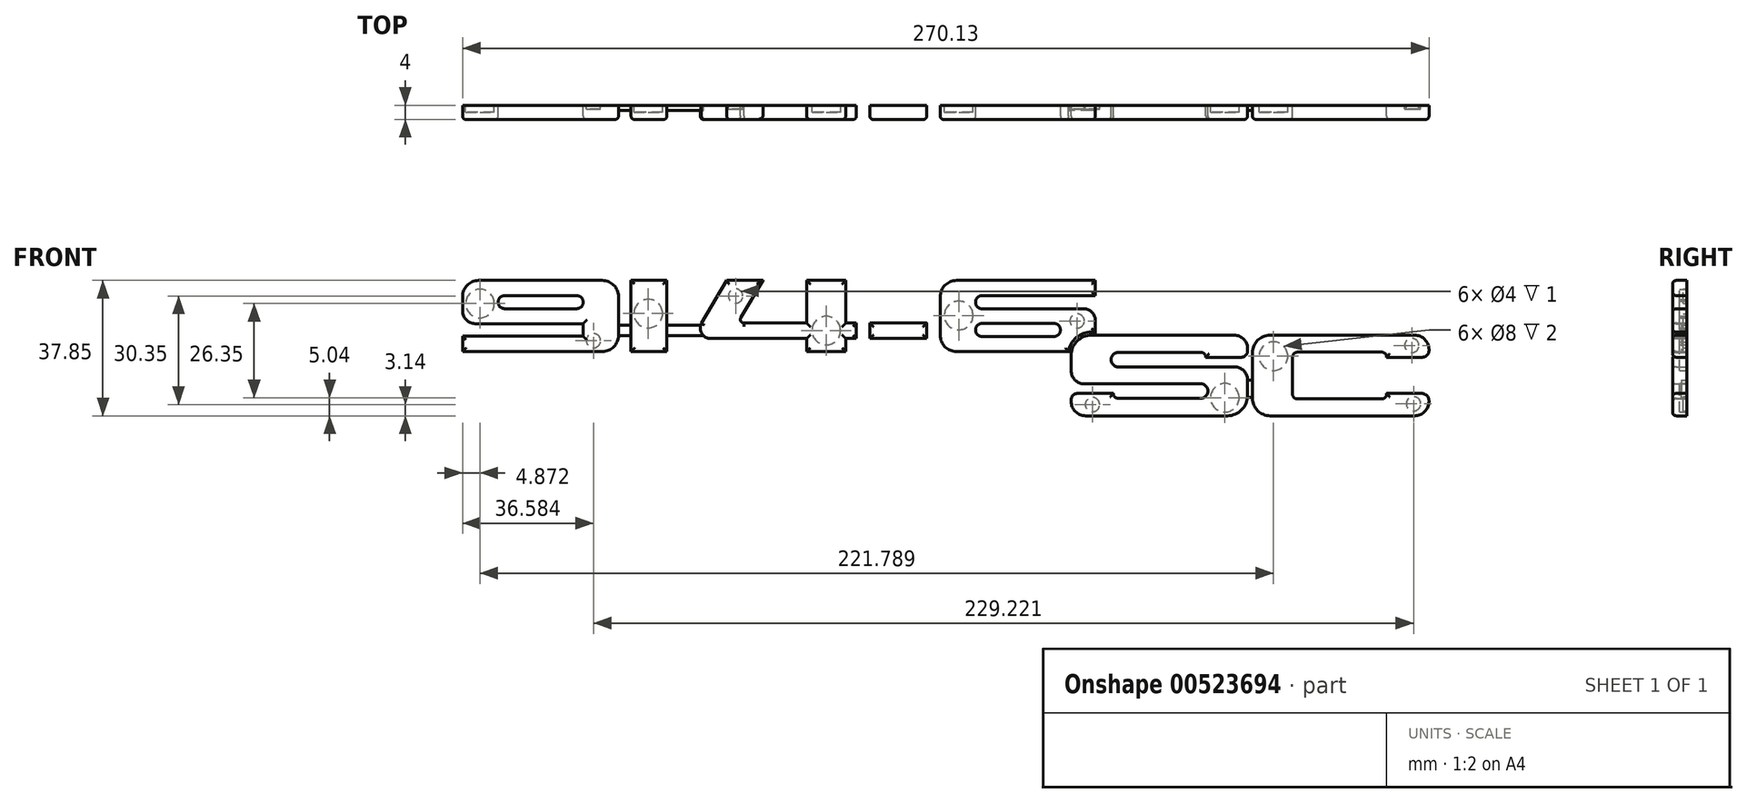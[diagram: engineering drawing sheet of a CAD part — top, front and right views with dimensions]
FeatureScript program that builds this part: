
annotation { "Feature Type Name" : "Feature", "Feature Type Description" : "" }
export const myFeature = defineFeature(function(context is Context, id is Id, definition is map)
    precondition{}
    {
        {
            var Q0;
            Q0=qCreatedBy(makeId("Front.planeOp"),FACE);
            var sketch = newSketch(context, id + "F0", { "sketchPlane" : qUnion([Q0])});
            skPoint(sketch, "E0", {"position": v(-109.13, 31.6) * mm});
            skPoint(sketch, "E1", {"position": v(-109.13, 11.72) * mm});
            skPoint(sketch, "E2", {"position": v(-65.54, 11.72) * mm});
            skPoint(sketch, "E3", {"position": v(-65.54, 31.6) * mm});
            skLineSegment(sketch, "E4.bottom", {"start": v(-104.63, 31.6) * mm, "end": v(-70.04, 31.6) * mm});
            skLineSegment(sketch, "E4.top", {"start": v(-109.13, 11.72) * mm, "end": v(-70.04, 11.72) * mm});
            skLineSegment(sketch, "E4.left", {"start": v(-109.13, 27.1) * mm, "end": v(-109.13, 23.04) * mm});
            skLineSegment(sketch, "E4.right", {"start": v(-65.54, 27.1) * mm, "end": v(-65.54, 16.22) * mm});
            skLineSegment(sketch, "E5.bottom", {"start": v(-109.13, 15.99) * mm, "end": v(-75.41, 15.99) * mm});
            skLineSegment(sketch, "E5.top", {"start": v(-105.62, 19.53) * mm, "end": v(-75.41, 19.53) * mm});
            skLineSegment(sketch, "E5.right", {"start": v(-75.41, 15.99) * mm, "end": v(-75.41, 19.53) * mm});
            skLineSegment(sketch, "E6.bottom", {"start": v(-77.15, 23.72) * mm, "end": v(-97.43, 23.72) * mm});
            skLineSegment(sketch, "E6.top", {"start": v(-77.15, 27.36) * mm, "end": v(-97.43, 27.36) * mm});
            skLineSegment(sketch, "E6.left", {"start": v(-75.41, 25.46) * mm, "end": v(-75.41, 25.62) * mm});
            skLineSegment(sketch, "E6.right", {"start": v(-99.16, 25.46) * mm, "end": v(-99.16, 25.62) * mm});
            skArc(sketch, "E7.filletArc", {"start": v(-104.63, 31.6) * mm, "mid": v(-107.81, 30.29) * mm, "end": v(-109.13, 27.1) * mm});
            skArc(sketch, "E8.filletArc", {"start": v(-65.54, 27.1) * mm, "mid": v(-66.86, 30.29) * mm, "end": v(-70.04, 31.6) * mm});
            skArc(sketch, "E9.filletArc", {"start": v(-70.04, 11.72) * mm, "mid": v(-66.86, 13.04) * mm, "end": v(-65.54, 16.22) * mm});
            skPoint(sketch, "E10.visualSharp", {"position": v(-99.16, 27.36) * mm});
            skArc(sketch, "E10.filletArc", {"start": v(-97.43, 27.36) * mm, "mid": v(-98.65, 26.85) * mm, "end": v(-99.16, 25.62) * mm});
            skPoint(sketch, "E11.visualSharp", {"position": v(-99.16, 23.72) * mm});
            skArc(sketch, "E11.filletArc", {"start": v(-99.16, 25.46) * mm, "mid": v(-98.65, 24.23) * mm, "end": v(-97.43, 23.72) * mm});
            skPoint(sketch, "E12.visualSharp", {"position": v(-75.41, 27.36) * mm});
            skArc(sketch, "E12.filletArc", {"start": v(-75.41, 25.62) * mm, "mid": v(-75.92, 26.85) * mm, "end": v(-77.15, 27.36) * mm});
            skPoint(sketch, "E13.visualSharp", {"position": v(-75.41, 23.72) * mm});
            skArc(sketch, "E13.filletArc", {"start": v(-77.15, 23.72) * mm, "mid": v(-75.92, 24.23) * mm, "end": v(-75.41, 25.46) * mm});
            skLineSegment(sketch, "E14.trimOffspring", {"start": v(-109.13, 15.99) * mm, "end": v(-109.13, 11.72) * mm});
            skPoint(sketch, "E15.visualSharp", {"position": v(-109.13, 19.53) * mm});
            skArc(sketch, "E15.filletArc", {"start": v(-109.13, 23.04) * mm, "mid": v(-108.1, 20.56) * mm, "end": v(-105.62, 19.53) * mm});
            skLineSegment(sketch, "E16", {"start": v(-62.04, 31.6) * mm, "end": v(-52.01, 31.6) * mm});
            skLineSegment(sketch, "E17", {"start": v(-62.04, 11.72) * mm, "end": v(-52.01, 11.72) * mm});
            skLineSegment(sketch, "E18.left", {"start": v(-62.04, 31.6) * mm, "end": v(-62.04, 11.72) * mm});
            skLineSegment(sketch, "E18.right", {"start": v(-52.01, 31.6) * mm, "end": v(-52.01, 11.72) * mm});
            skLineSegment(sketch, "E19", {"start": v(-31.25, 31.6) * mm, "end": v(-25.18, 31.6) * mm});
            skLineSegment(sketch, "E20.bottom", {"start": v(-12.94, 31.6) * mm, "end": v(-2.03, 31.6) * mm});
            skLineSegment(sketch, "E20.top", {"start": v(-12.94, 11.72) * mm, "end": v(-2.03, 11.72) * mm});
            skLineSegment(sketch, "E20.left", {"start": v(-12.94, 31.6) * mm, "end": v(-12.94, 19.68) * mm});
            skLineSegment(sketch, "E20.right", {"start": v(-2.03, 31.6) * mm, "end": v(-2.03, 19.68) * mm});
            skLineSegment(sketch, "E21.bottom", {"start": v(0.96, 19.68) * mm, "end": v(-2.03, 19.68) * mm});
            skLineSegment(sketch, "E21.top", {"start": v(0.96, 15.35) * mm, "end": v(-2.03, 15.35) * mm});
            skLineSegment(sketch, "E21.left", {"start": v(0.96, 19.68) * mm, "end": v(0.96, 15.35) * mm});
            skLineSegment(sketch, "E22", {"start": v(-35.26, 31.6) * mm, "end": v(-42.35, 19.59) * mm});
            skLineSegment(sketch, "E23", {"start": v(-25.18, 31.6) * mm, "end": v(-31.35, 21.25) * mm});
            skPoint(sketch, "E24", {"position": v(-30.43, 19.68) * mm});
            skLineSegment(sketch, "E25.trimOffspring", {"start": v(-12.94, 15.35) * mm, "end": v(-12.94, 11.72) * mm});
            skLineSegment(sketch, "E26.trimOffspring", {"start": v(-12.94, 15.35) * mm, "end": v(-39.77, 15.35) * mm});
            skLineSegment(sketch, "E27.trimOffspring", {"start": v(-2.03, 15.35) * mm, "end": v(-2.03, 11.72) * mm});
            skLineSegment(sketch, "E28.trimOffspring", {"start": v(-12.94, 19.68) * mm, "end": v(-30.43, 19.68) * mm});
            skLineSegment(sketch, "E29.trimOffspring", {"start": v(-35.26, 31.6) * mm, "end": v(-31.25, 31.6) * mm});
            skArc(sketch, "E30", {"start": v(-42.35, 19.59) * mm, "mid": v(-42.25, 16.75) * mm, "end": v(-39.77, 15.35) * mm});
            skArc(sketch, "E31", {"start": v(-31.35, 21.25) * mm, "mid": v(-31.35, 20.2) * mm, "end": v(-30.43, 19.68) * mm});
            skLineSegment(sketch, "E32", {"start": v(28.93, 31.6) * mm, "end": v(67.75, 31.6) * mm});
            skLineSegment(sketch, "E33", {"start": v(28.93, 11.72) * mm, "end": v(60.09, 11.72) * mm});
            skLineSegment(sketch, "E34.bottom", {"start": v(4.7, 19.69) * mm, "end": v(20.61, 19.69) * mm});
            skLineSegment(sketch, "E34.top", {"start": v(4.7, 15.35) * mm, "end": v(20.61, 15.35) * mm});
            skLineSegment(sketch, "E34.left", {"start": v(4.7, 19.69) * mm, "end": v(4.7, 15.35) * mm});
            skLineSegment(sketch, "E34.right", {"start": v(20.61, 19.69) * mm, "end": v(20.61, 15.35) * mm});
            skLineSegment(sketch, "E35", {"start": v(24.38, 26.4) * mm, "end": v(24.38, 16.28) * mm});
            skLineSegment(sketch, "E36", {"start": v(24.38, 26.4) * mm, "end": v(24.38, 27.06) * mm});
            skLineSegment(sketch, "E37", {"start": v(67.75, 31.6) * mm, "end": v(67.75, 27.39) * mm});
            skLineSegment(sketch, "E38.bottom", {"start": v(67.75, 27.39) * mm, "end": v(36.1, 27.39) * mm});
            skLineSegment(sketch, "E38.top", {"start": v(64.5, 23.67) * mm, "end": v(36.1, 23.67) * mm});
            skLineSegment(sketch, "E38.right", {"start": v(34.28, 25.56) * mm, "end": v(34.28, 25.5) * mm});
            skLineSegment(sketch, "E39.bottom", {"start": v(36.1, 19.61) * mm, "end": v(56.17, 19.61) * mm});
            skLineSegment(sketch, "E39.top", {"start": v(36.1, 15.93) * mm, "end": v(56.17, 15.93) * mm});
            skLineSegment(sketch, "E39.left", {"start": v(34.28, 17.78) * mm, "end": v(34.28, 17.76) * mm});
            skLineSegment(sketch, "E39.right", {"start": v(58, 17.78) * mm, "end": v(58, 17.76) * mm});
            skLineSegment(sketch, "E40.trimOffspring", {"start": v(67.75, 20.42) * mm, "end": v(67.75, 17.15) * mm});
            skPoint(sketch, "E41.visualSharp", {"position": v(24.38, 31.6) * mm});
            skArc(sketch, "E41.filletArc", {"start": v(28.93, 31.6) * mm, "mid": v(25.71, 30.27) * mm, "end": v(24.38, 27.06) * mm});
            skPoint(sketch, "E42.visualSharp", {"position": v(24.38, 11.72) * mm});
            skArc(sketch, "E42.filletArc", {"start": v(24.38, 16.28) * mm, "mid": v(25.71, 13.06) * mm, "end": v(28.93, 11.72) * mm});
            skPoint(sketch, "E43.visualSharp", {"position": v(67.75, 23.67) * mm});
            skArc(sketch, "E43.filletArc", {"start": v(67.75, 20.42) * mm, "mid": v(66.8, 22.72) * mm, "end": v(64.5, 23.67) * mm});
            skPoint(sketch, "E44.visualSharp", {"position": v(34.28, 27.39) * mm});
            skArc(sketch, "E44.filletArc", {"start": v(36.1, 27.39) * mm, "mid": v(34.81, 26.85) * mm, "end": v(34.28, 25.56) * mm});
            skPoint(sketch, "E45.visualSharp", {"position": v(34.28, 23.67) * mm});
            skArc(sketch, "E45.filletArc", {"start": v(34.28, 25.5) * mm, "mid": v(34.81, 24.21) * mm, "end": v(36.1, 23.67) * mm});
            skPoint(sketch, "E46.visualSharp", {"position": v(34.28, 19.61) * mm});
            skArc(sketch, "E46.filletArc", {"start": v(36.1, 19.61) * mm, "mid": v(34.81, 19.08) * mm, "end": v(34.28, 17.78) * mm});
            skPoint(sketch, "E47.visualSharp", {"position": v(34.28, 15.93) * mm});
            skArc(sketch, "E47.filletArc", {"start": v(34.28, 17.76) * mm, "mid": v(34.81, 16.47) * mm, "end": v(36.1, 15.93) * mm});
            skPoint(sketch, "E48.visualSharp", {"position": v(58, 19.61) * mm});
            skArc(sketch, "E48.filletArc", {"start": v(58, 17.78) * mm, "mid": v(57.46, 19.08) * mm, "end": v(56.17, 19.61) * mm});
            skPoint(sketch, "E49.visualSharp", {"position": v(58, 15.93) * mm});
            skArc(sketch, "E49.filletArc", {"start": v(56.17, 15.93) * mm, "mid": v(57.46, 16.47) * mm, "end": v(58, 17.76) * mm});
            skLineSegment(sketch, "E50", {"start": v(60.97, -1.92) * mm, "end": v(60.97, -1.8) * mm});
            skPoint(sketch, "E50.endSnap0", {"position": v(57.46, 16.47) * mm});
            skLineSegment(sketch, "E51", {"start": v(60.97, -1.92) * mm, "end": v(60.97, -2.2) * mm});
            skLineSegment(sketch, "E52", {"start": v(67.38, -6.24) * mm, "end": v(65.01, -6.24) * mm});
            skLineSegment(sketch, "E53", {"start": v(67.38, -6.24) * mm, "end": v(104.63, -6.24) * mm});
            skLineSegment(sketch, "E54", {"start": v(78.67, 16.3) * mm, "end": v(66.63, 16.3) * mm});
            skLineSegment(sketch, "E55", {"start": v(78.67, 16.3) * mm, "end": v(106.59, 16.3) * mm});
            skLineSegment(sketch, "E56", {"start": v(110.29, 2.56) * mm, "end": v(110.29, -0.58) * mm});
            skLineSegment(sketch, "E57", {"start": v(110.29, 2.56) * mm, "end": v(110.29, 3.72) * mm});
            skLineSegment(sketch, "E58", {"start": v(62.77, 0) * mm, "end": v(72.74, 0) * mm});
            skLineSegment(sketch, "E59", {"start": v(83.02, -1.35) * mm, "end": v(74.07, -1.35) * mm});
            skLineSegment(sketch, "E60", {"start": v(83.02, -1.35) * mm, "end": v(97.22, -1.35) * mm});
            skLineSegment(sketch, "E61", {"start": v(81.85, 2.69) * mm, "end": v(64.67, 2.69) * mm});
            skLineSegment(sketch, "E62", {"start": v(81.85, 2.69) * mm, "end": v(97.22, 2.69) * mm});
            skLineSegment(sketch, "E63", {"start": v(86.84, 7.43) * mm, "end": v(74.15, 7.43) * mm});
            skLineSegment(sketch, "E64", {"start": v(86.84, 7.43) * mm, "end": v(106.59, 7.43) * mm});
            skLineSegment(sketch, "E65", {"start": v(83.16, 11.49) * mm, "end": v(74.15, 11.49) * mm});
            skLineSegment(sketch, "E66", {"start": v(83.16, 11.49) * mm, "end": v(97.27, 11.49) * mm});
            skLineSegment(sketch, "E67", {"start": v(107, 10.1) * mm, "end": v(98.63, 10.1) * mm});
            skLineSegment(sketch, "E68", {"start": v(107, 10.1) * mm, "end": v(108.44, 10.1) * mm});
            skLineSegment(sketch, "E69", {"start": v(98.63, 10.1) * mm, "end": v(98.63, 10.12) * mm});
            skLineSegment(sketch, "E70.trimOffspring", {"start": v(110.29, 11.96) * mm, "end": v(110.29, 12.6) * mm});
            skLineSegment(sketch, "E71.trimOffspring", {"start": v(60.97, 6.39) * mm, "end": v(60.97, 10.64) * mm});
            skPoint(sketch, "E72.orphan", {"position": v(58.48, 0) * mm});
            skPoint(sketch, "E73.orphan", {"position": v(60.97, -7.6) * mm});
            skLineSegment(sketch, "E74", {"start": v(72.74, 0) * mm, "end": v(72.74, -0.02) * mm});
            skPoint(sketch, "E75.visualSharp", {"position": v(60.97, 16.3) * mm});
            skArc(sketch, "E75.filletArc", {"start": v(66.63, 16.3) * mm, "mid": v(62.63, 14.65) * mm, "end": v(60.97, 10.64) * mm});
            skPoint(sketch, "E76.visualSharp", {"position": v(110.29, -6.24) * mm});
            skArc(sketch, "E76.filletArc", {"start": v(104.63, -6.24) * mm, "mid": v(108.63, -4.58) * mm, "end": v(110.29, -0.58) * mm});
            skPoint(sketch, "E77.visualSharp", {"position": v(60.97, -6.24) * mm});
            skArc(sketch, "E77.filletArc", {"start": v(60.97, -2.2) * mm, "mid": v(62.16, -5.06) * mm, "end": v(65.01, -6.24) * mm});
            skPoint(sketch, "E78.visualSharp", {"position": v(110.29, 16.3) * mm});
            skArc(sketch, "E78.filletArc", {"start": v(110.29, 12.6) * mm, "mid": v(109.2, 15.22) * mm, "end": v(106.59, 16.3) * mm});
            skPoint(sketch, "E79.visualSharp", {"position": v(110.29, 7.43) * mm});
            skArc(sketch, "E79.filletArc", {"start": v(110.29, 3.72) * mm, "mid": v(109.2, 6.34) * mm, "end": v(106.59, 7.43) * mm});
            skPoint(sketch, "E80.visualSharp", {"position": v(60.97, 2.69) * mm});
            skArc(sketch, "E80.filletArc", {"start": v(60.97, 6.39) * mm, "mid": v(62.06, 3.77) * mm, "end": v(64.67, 2.69) * mm});
            skPoint(sketch, "E81.visualSharp", {"position": v(60.97, 0) * mm});
            skArc(sketch, "E81.filletArc", {"start": v(62.77, 0) * mm, "mid": v(61.5, -0.53) * mm, "end": v(60.97, -1.8) * mm});
            skPoint(sketch, "E82.visualSharp", {"position": v(110.29, 10.1) * mm});
            skArc(sketch, "E82.filletArc", {"start": v(108.44, 10.1) * mm, "mid": v(109.75, 10.65) * mm, "end": v(110.29, 11.96) * mm});
            skLineSegment(sketch, "E83", {"start": v(72.17, 9.5) * mm, "end": v(72.17, 9.4) * mm});
            skPoint(sketch, "E84.visualSharp", {"position": v(72.17, 11.49) * mm});
            skArc(sketch, "E84.filletArc", {"start": v(74.15, 11.49) * mm, "mid": v(72.75, 10.9) * mm, "end": v(72.17, 9.5) * mm});
            skPoint(sketch, "E85.visualSharp", {"position": v(72.17, 7.43) * mm});
            skArc(sketch, "E85.filletArc", {"start": v(72.17, 9.4) * mm, "mid": v(72.75, 8) * mm, "end": v(74.15, 7.43) * mm});
            skLineSegment(sketch, "E86", {"start": v(99.2, 0.7) * mm, "end": v(99.2, 0.63) * mm});
            skPoint(sketch, "E87.visualSharp", {"position": v(99.2, 2.69) * mm});
            skArc(sketch, "E87.filletArc", {"start": v(99.2, 0.7) * mm, "mid": v(98.63, 2.1) * mm, "end": v(97.22, 2.69) * mm});
            skPoint(sketch, "E88.visualSharp", {"position": v(99.2, -1.35) * mm});
            skArc(sketch, "E88.filletArc", {"start": v(97.22, -1.35) * mm, "mid": v(98.63, -0.77) * mm, "end": v(99.2, 0.63) * mm});
            skPoint(sketch, "E89.visualSharp", {"position": v(72.74, -1.35) * mm});
            skArc(sketch, "E89.filletArc", {"start": v(72.74, -0.02) * mm, "mid": v(73.13, -0.96) * mm, "end": v(74.07, -1.35) * mm});
            skPoint(sketch, "E90.visualSharp", {"position": v(98.63, 11.49) * mm});
            skArc(sketch, "E90.filletArc", {"start": v(98.63, 10.12) * mm, "mid": v(98.23, 11.09) * mm, "end": v(97.27, 11.49) * mm});
            skPoint(sketch, "E91", {"position": v(111.66, 16.3) * mm});
            skPoint(sketch, "E92", {"position": v(111.66, -6.24) * mm});
            skPoint(sketch, "E93", {"position": v(161, -6.24) * mm});
            skPoint(sketch, "E94", {"position": v(161, 16.3) * mm});
            skLineSegment(sketch, "E95.bottom", {"start": v(116.55, 16.3) * mm, "end": v(156.97, 16.3) * mm});
            skLineSegment(sketch, "E95.top", {"start": v(116.55, -6.24) * mm, "end": v(156.97, -6.24) * mm});
            skLineSegment(sketch, "E95.left", {"start": v(111.66, 11.41) * mm, "end": v(111.66, -1.35) * mm});
            skLineSegment(sketch, "E95.right", {"start": v(161, 12.27) * mm, "end": v(161, 11.93) * mm});
            skLineSegment(sketch, "E96", {"start": v(122.87, 5.48) * mm, "end": v(122.87, 10.24) * mm});
            skLineSegment(sketch, "E97", {"start": v(158.97, 0) * mm, "end": v(149.12, 0) * mm});
            skLineSegment(sketch, "E98", {"start": v(157.34, 10.13) * mm, "end": v(149.12, 10.13) * mm});
            skLineSegment(sketch, "E99", {"start": v(157.34, 10.13) * mm, "end": v(159.2, 10.13) * mm});
            skLineSegment(sketch, "E100", {"start": v(139.85, 11.56) * mm, "end": v(124.18, 11.56) * mm});
            skLineSegment(sketch, "E101", {"start": v(139.85, 11.56) * mm, "end": v(147.8, 11.56) * mm});
            skLineSegment(sketch, "E102", {"start": v(149.12, 10.13) * mm, "end": v(149.12, 10.24) * mm});
            skLineSegment(sketch, "E103.trimOffspring", {"start": v(161, -2.03) * mm, "end": v(161, -2.21) * mm});
            skArc(sketch, "E104.filletArc", {"start": v(116.55, 16.3) * mm, "mid": v(113.1, 14.87) * mm, "end": v(111.66, 11.41) * mm});
            skArc(sketch, "E105.filletArc", {"start": v(111.66, -1.35) * mm, "mid": v(113.1, -4.8) * mm, "end": v(116.55, -6.24) * mm});
            skArc(sketch, "E106.filletArc", {"start": v(161, 12.27) * mm, "mid": v(159.82, 15.12) * mm, "end": v(156.97, 16.3) * mm});
            skArc(sketch, "E107.filletArc", {"start": v(156.97, -6.24) * mm, "mid": v(159.82, -5.06) * mm, "end": v(161, -2.21) * mm});
            skPoint(sketch, "E108.visualSharp", {"position": v(161, 10.13) * mm});
            skArc(sketch, "E108.filletArc", {"start": v(159.2, 10.13) * mm, "mid": v(160.48, 10.66) * mm, "end": v(161, 11.93) * mm});
            skPoint(sketch, "E109.visualSharp", {"position": v(161, 0) * mm});
            skArc(sketch, "E109.filletArc", {"start": v(161, -2.03) * mm, "mid": v(160.4, -0.6) * mm, "end": v(158.97, 0) * mm});
            skLineSegment(sketch, "E110", {"start": v(122.87, 5.48) * mm, "end": v(122.87, -0.2) * mm});
            skLineSegment(sketch, "E111", {"start": v(129.73, -1.52) * mm, "end": v(124.18, -1.52) * mm});
            skLineSegment(sketch, "E112", {"start": v(129.73, -1.52) * mm, "end": v(147.8, -1.52) * mm});
            skLineSegment(sketch, "E113", {"start": v(149.12, 0) * mm, "end": v(149.12, -0.2) * mm});
            skPoint(sketch, "E114.visualSharp", {"position": v(149.12, 11.56) * mm});
            skArc(sketch, "E114.filletArc", {"start": v(149.12, 10.24) * mm, "mid": v(148.73, 11.17) * mm, "end": v(147.8, 11.56) * mm});
            skPoint(sketch, "E115.visualSharp", {"position": v(149.12, -1.52) * mm});
            skArc(sketch, "E115.filletArc", {"start": v(147.8, -1.52) * mm, "mid": v(148.73, -1.14) * mm, "end": v(149.12, -0.2) * mm});
            skPoint(sketch, "E116.visualSharp", {"position": v(122.87, 11.56) * mm});
            skArc(sketch, "E116.filletArc", {"start": v(124.18, 11.56) * mm, "mid": v(123.25, 11.17) * mm, "end": v(122.87, 10.24) * mm});
            skPoint(sketch, "E117.visualSharp", {"position": v(122.87, -1.52) * mm});
            skArc(sketch, "E117.filletArc", {"start": v(122.87, -0.2) * mm, "mid": v(123.25, -1.14) * mm, "end": v(124.18, -1.52) * mm});
            skLineSegment(sketch, "E118", {"start": v(-0.53, 19.68) * mm, "end": v(0.96, 19.68) * mm});
            skLineSegment(sketch, "E119", {"start": v(-0.33, 15.35) * mm, "end": v(0.96, 15.35) * mm});
            skPoint(sketch, "E120", {"position": v(67.75, 16.3) * mm});
            skPoint(sketch, "E121", {"position": v(61.08, 11.72) * mm});
            skArc(sketch, "E122.0", {"start": v(66.63, 17.15) * mm, "mid": v(62.43, 15.61) * mm, "end": v(60.21, 11.72) * mm});
            skLineSegment(sketch, "E122.1", {"start": v(67.75, 17.15) * mm, "end": v(66.63, 17.15) * mm});
            skLineSegment(sketch, "E123", {"start": v(59.83, 11.72) * mm, "end": v(60.21, 11.72) * mm});
            skSolve(sketch);
        }
        {
            var Q0;
            Q0=qCreatedBy(makeId("Front.planeOp"),FACE);
            var sketch = newSketch(context, id + "F1", { "sketchPlane" : qUnion([Q0])});
            skPoint(sketch, "E124.0", {"position": v(-109.13, 31.6) * mm});
            skPoint(sketch, "E124.1", {"position": v(-109.13, 11.72) * mm});
            skPoint(sketch, "E124.2", {"position": v(-65.54, 11.72) * mm});
            skPoint(sketch, "E124.3", {"position": v(-65.54, 31.6) * mm});
            skLineSegment(sketch, "E124.4", {"start": v(-104.63, 31.6) * mm, "end": v(-70.04, 31.6) * mm});
            skLineSegment(sketch, "E124.5", {"start": v(-109.13, 11.72) * mm, "end": v(-70.04, 11.72) * mm});
            skLineSegment(sketch, "E124.6", {"start": v(-109.13, 27.1) * mm, "end": v(-109.13, 23.04) * mm});
            skLineSegment(sketch, "E124.7", {"start": v(-65.54, 27.1) * mm, "end": v(-65.54, 16.22) * mm});
            skLineSegment(sketch, "E124.8", {"start": v(-109.13, 15.99) * mm, "end": v(-75.41, 15.99) * mm});
            skLineSegment(sketch, "E124.9", {"start": v(-105.62, 19.53) * mm, "end": v(-75.41, 19.53) * mm});
            skLineSegment(sketch, "E124.10", {"start": v(-75.41, 15.99) * mm, "end": v(-75.41, 19.53) * mm});
            skLineSegment(sketch, "E124.11", {"start": v(-77.15, 23.72) * mm, "end": v(-97.43, 23.72) * mm});
            skLineSegment(sketch, "E124.12", {"start": v(-77.15, 27.36) * mm, "end": v(-97.43, 27.36) * mm});
            skLineSegment(sketch, "E124.13", {"start": v(-75.41, 25.46) * mm, "end": v(-75.41, 25.62) * mm});
            skLineSegment(sketch, "E124.14", {"start": v(-99.16, 25.46) * mm, "end": v(-99.16, 25.62) * mm});
            skPoint(sketch, "E124.15", {"position": v(-109.13, 31.6) * mm});
            skArc(sketch, "E124.16", {"start": v(-104.63, 31.6) * mm, "mid": v(-107.81, 30.29) * mm, "end": v(-109.13, 27.1) * mm});
            skPoint(sketch, "E124.17", {"position": v(-65.54, 31.6) * mm});
            skArc(sketch, "E124.18", {"start": v(-65.54, 27.1) * mm, "mid": v(-66.86, 30.29) * mm, "end": v(-70.04, 31.6) * mm});
            skPoint(sketch, "E124.19", {"position": v(-65.54, 11.72) * mm});
            skArc(sketch, "E124.20", {"start": v(-70.04, 11.72) * mm, "mid": v(-66.86, 13.04) * mm, "end": v(-65.54, 16.22) * mm});
            skPoint(sketch, "E124.21", {"position": v(-99.16, 27.36) * mm});
            skArc(sketch, "E124.22", {"start": v(-97.43, 27.36) * mm, "mid": v(-98.65, 26.85) * mm, "end": v(-99.16, 25.62) * mm});
            skPoint(sketch, "E124.23", {"position": v(-99.16, 23.72) * mm});
            skArc(sketch, "E124.24", {"start": v(-99.16, 25.46) * mm, "mid": v(-98.65, 24.23) * mm, "end": v(-97.43, 23.72) * mm});
            skPoint(sketch, "E124.25", {"position": v(-75.41, 27.36) * mm});
            skArc(sketch, "E124.26", {"start": v(-75.41, 25.62) * mm, "mid": v(-75.92, 26.85) * mm, "end": v(-77.15, 27.36) * mm});
            skPoint(sketch, "E124.27", {"position": v(-75.41, 23.72) * mm});
            skArc(sketch, "E124.28", {"start": v(-77.15, 23.72) * mm, "mid": v(-75.92, 24.23) * mm, "end": v(-75.41, 25.46) * mm});
            skLineSegment(sketch, "E124.29", {"start": v(-109.13, 15.99) * mm, "end": v(-109.13, 11.72) * mm});
            skPoint(sketch, "E124.30", {"position": v(-109.13, 19.53) * mm});
            skArc(sketch, "E124.31", {"start": v(-109.13, 23.04) * mm, "mid": v(-108.1, 20.56) * mm, "end": v(-105.62, 19.53) * mm});
            skLineSegment(sketch, "E124.32", {"start": v(-62.04, 31.6) * mm, "end": v(-52.01, 31.6) * mm});
            skLineSegment(sketch, "E124.33", {"start": v(-62.04, 11.72) * mm, "end": v(-52.01, 11.72) * mm});
            skLineSegment(sketch, "E124.34", {"start": v(-62.04, 31.6) * mm, "end": v(-52.01, 31.6) * mm});
            skLineSegment(sketch, "E124.35", {"start": v(-62.04, 11.72) * mm, "end": v(-52.01, 11.72) * mm});
            skLineSegment(sketch, "E124.36", {"start": v(-62.04, 31.6) * mm, "end": v(-62.04, 11.72) * mm});
            skLineSegment(sketch, "E124.37", {"start": v(-52.01, 31.6) * mm, "end": v(-52.01, 11.72) * mm});
            skLineSegment(sketch, "E124.38", {"start": v(-31.25, 31.6) * mm, "end": v(-25.18, 31.6) * mm});
            skLineSegment(sketch, "E124.39", {"start": v(-12.94, 31.6) * mm, "end": v(-2.03, 31.6) * mm});
            skLineSegment(sketch, "E124.40", {"start": v(-12.94, 11.72) * mm, "end": v(-2.03, 11.72) * mm});
            skLineSegment(sketch, "E124.41", {"start": v(-12.94, 31.6) * mm, "end": v(-12.94, 19.68) * mm});
            skLineSegment(sketch, "E124.42", {"start": v(-2.03, 31.6) * mm, "end": v(-2.03, 19.68) * mm});
            skLineSegment(sketch, "E124.43", {"start": v(0.96, 19.68) * mm, "end": v(-2.03, 19.68) * mm});
            skLineSegment(sketch, "E124.44", {"start": v(0.96, 15.35) * mm, "end": v(-2.03, 15.35) * mm});
            skLineSegment(sketch, "E124.45", {"start": v(0.96, 19.68) * mm, "end": v(0.96, 15.35) * mm});
            skLineSegment(sketch, "E124.46", {"start": v(-35.26, 31.6) * mm, "end": v(-42.35, 19.59) * mm});
            skLineSegment(sketch, "E124.47", {"start": v(-25.18, 31.6) * mm, "end": v(-31.35, 21.25) * mm});
            skPoint(sketch, "E124.48", {"position": v(-30.43, 19.68) * mm});
            skLineSegment(sketch, "E124.49", {"start": v(-12.94, 15.35) * mm, "end": v(-12.94, 11.72) * mm});
            skLineSegment(sketch, "E124.50", {"start": v(-12.94, 15.35) * mm, "end": v(-39.77, 15.35) * mm});
            skLineSegment(sketch, "E124.51", {"start": v(-2.03, 15.35) * mm, "end": v(-2.03, 11.72) * mm});
            skLineSegment(sketch, "E124.52", {"start": v(-12.94, 19.68) * mm, "end": v(-30.43, 19.68) * mm});
            skLineSegment(sketch, "E124.53", {"start": v(-12.94, 11.72) * mm, "end": v(-2.03, 11.72) * mm});
            skLineSegment(sketch, "E124.54", {"start": v(-12.94, 31.6) * mm, "end": v(-2.03, 31.6) * mm});
            skLineSegment(sketch, "E124.55", {"start": v(-35.26, 31.6) * mm, "end": v(-31.25, 31.6) * mm});
            skArc(sketch, "E124.56", {"start": v(-42.35, 19.59) * mm, "mid": v(-42.25, 16.75) * mm, "end": v(-39.77, 15.35) * mm});
            skArc(sketch, "E124.57", {"start": v(-31.35, 21.25) * mm, "mid": v(-31.35, 20.2) * mm, "end": v(-30.43, 19.68) * mm});
            skLineSegment(sketch, "E124.58", {"start": v(28.93, 31.6) * mm, "end": v(67.75, 31.6) * mm});
            skLineSegment(sketch, "E124.59", {"start": v(28.93, 11.72) * mm, "end": v(60.09, 11.72) * mm});
            skLineSegment(sketch, "E124.60", {"start": v(4.7, 19.69) * mm, "end": v(20.61, 19.69) * mm});
            skLineSegment(sketch, "E124.61", {"start": v(4.7, 15.35) * mm, "end": v(20.61, 15.35) * mm});
            skLineSegment(sketch, "E124.62", {"start": v(4.7, 19.69) * mm, "end": v(4.7, 15.35) * mm});
            skLineSegment(sketch, "E124.63", {"start": v(20.61, 19.69) * mm, "end": v(20.61, 15.35) * mm});
            skLineSegment(sketch, "E124.64", {"start": v(24.38, 26.4) * mm, "end": v(24.38, 16.28) * mm});
            skLineSegment(sketch, "E124.65", {"start": v(24.38, 26.4) * mm, "end": v(24.38, 27.06) * mm});
            skLineSegment(sketch, "E124.66", {"start": v(67.75, 31.6) * mm, "end": v(67.75, 27.39) * mm});
            skLineSegment(sketch, "E124.67", {"start": v(67.75, 27.39) * mm, "end": v(36.1, 27.39) * mm});
            skLineSegment(sketch, "E124.68", {"start": v(64.5, 23.67) * mm, "end": v(36.1, 23.67) * mm});
            skLineSegment(sketch, "E124.69", {"start": v(34.28, 25.56) * mm, "end": v(34.28, 25.5) * mm});
            skLineSegment(sketch, "E124.70", {"start": v(36.1, 19.61) * mm, "end": v(56.17, 19.61) * mm});
            skLineSegment(sketch, "E124.71", {"start": v(36.1, 15.93) * mm, "end": v(56.17, 15.93) * mm});
            skLineSegment(sketch, "E124.72", {"start": v(34.28, 17.78) * mm, "end": v(34.28, 17.76) * mm});
            skLineSegment(sketch, "E124.73", {"start": v(58, 17.78) * mm, "end": v(58, 17.76) * mm});
            skLineSegment(sketch, "E124.74", {"start": v(67.75, 20.42) * mm, "end": v(67.75, 17.15) * mm});
            skPoint(sketch, "E124.77", {"position": v(24.38, 31.6) * mm});
            skArc(sketch, "E124.78", {"start": v(28.93, 31.6) * mm, "mid": v(25.71, 30.27) * mm, "end": v(24.38, 27.06) * mm});
            skPoint(sketch, "E124.79", {"position": v(24.38, 11.72) * mm});
            skArc(sketch, "E124.80", {"start": v(24.38, 16.28) * mm, "mid": v(25.71, 13.06) * mm, "end": v(28.93, 11.72) * mm});
            skPoint(sketch, "E124.81", {"position": v(67.75, 23.67) * mm});
            skArc(sketch, "E124.82", {"start": v(67.75, 20.42) * mm, "mid": v(66.8, 22.72) * mm, "end": v(64.5, 23.67) * mm});
            skPoint(sketch, "E124.83", {"position": v(34.28, 27.39) * mm});
            skArc(sketch, "E124.84", {"start": v(36.1, 27.39) * mm, "mid": v(34.81, 26.85) * mm, "end": v(34.28, 25.56) * mm});
            skPoint(sketch, "E124.85", {"position": v(34.28, 23.67) * mm});
            skArc(sketch, "E124.86", {"start": v(34.28, 25.5) * mm, "mid": v(34.81, 24.21) * mm, "end": v(36.1, 23.67) * mm});
            skPoint(sketch, "E124.87", {"position": v(34.28, 19.61) * mm});
            skArc(sketch, "E124.88", {"start": v(36.1, 19.61) * mm, "mid": v(34.81, 19.08) * mm, "end": v(34.28, 17.78) * mm});
            skPoint(sketch, "E124.89", {"position": v(34.28, 15.93) * mm});
            skArc(sketch, "E124.90", {"start": v(34.28, 17.76) * mm, "mid": v(34.81, 16.47) * mm, "end": v(36.1, 15.93) * mm});
            skPoint(sketch, "E124.91", {"position": v(58, 19.61) * mm});
            skArc(sketch, "E124.92", {"start": v(58, 17.78) * mm, "mid": v(57.46, 19.08) * mm, "end": v(56.17, 19.61) * mm});
            skPoint(sketch, "E124.93", {"position": v(58, 15.93) * mm});
            skArc(sketch, "E124.94", {"start": v(56.17, 15.93) * mm, "mid": v(57.46, 16.47) * mm, "end": v(58, 17.76) * mm});
            skLineSegment(sketch, "E124.95", {"start": v(60.97, -1.92) * mm, "end": v(60.97, -1.8) * mm});
            skPoint(sketch, "E124.96", {"position": v(57.46, 16.47) * mm});
            skLineSegment(sketch, "E124.97", {"start": v(60.97, -1.92) * mm, "end": v(60.97, -2.2) * mm});
            skLineSegment(sketch, "E124.98", {"start": v(67.38, -6.24) * mm, "end": v(65.01, -6.24) * mm});
            skLineSegment(sketch, "E124.99", {"start": v(67.38, -6.24) * mm, "end": v(104.63, -6.24) * mm});
            skLineSegment(sketch, "E124.100", {"start": v(78.67, 16.3) * mm, "end": v(66.63, 16.3) * mm});
            skLineSegment(sketch, "E124.101", {"start": v(78.67, 16.3) * mm, "end": v(106.59, 16.3) * mm});
            skLineSegment(sketch, "E124.102", {"start": v(110.29, 2.56) * mm, "end": v(110.29, -0.58) * mm});
            skLineSegment(sketch, "E124.103", {"start": v(110.29, 2.56) * mm, "end": v(110.29, 3.72) * mm});
            skLineSegment(sketch, "E124.104", {"start": v(62.77, 0) * mm, "end": v(72.74, 0) * mm});
            skLineSegment(sketch, "E124.105", {"start": v(83.02, -1.35) * mm, "end": v(74.07, -1.35) * mm});
            skLineSegment(sketch, "E124.106", {"start": v(83.02, -1.35) * mm, "end": v(97.22, -1.35) * mm});
            skLineSegment(sketch, "E124.107", {"start": v(81.85, 2.69) * mm, "end": v(64.67, 2.69) * mm});
            skLineSegment(sketch, "E124.108", {"start": v(81.85, 2.69) * mm, "end": v(97.22, 2.69) * mm});
            skLineSegment(sketch, "E124.109", {"start": v(86.84, 7.43) * mm, "end": v(74.15, 7.43) * mm});
            skLineSegment(sketch, "E124.110", {"start": v(86.84, 7.43) * mm, "end": v(106.59, 7.43) * mm});
            skLineSegment(sketch, "E124.111", {"start": v(83.16, 11.49) * mm, "end": v(74.15, 11.49) * mm});
            skLineSegment(sketch, "E124.112", {"start": v(83.16, 11.49) * mm, "end": v(97.27, 11.49) * mm});
            skLineSegment(sketch, "E124.113", {"start": v(107, 10.1) * mm, "end": v(98.63, 10.1) * mm});
            skLineSegment(sketch, "E124.114", {"start": v(107, 10.1) * mm, "end": v(108.44, 10.1) * mm});
            skLineSegment(sketch, "E124.115", {"start": v(98.63, 10.1) * mm, "end": v(98.63, 10.12) * mm});
            skLineSegment(sketch, "E124.116", {"start": v(110.29, 11.96) * mm, "end": v(110.29, 12.6) * mm});
            skLineSegment(sketch, "E124.117", {"start": v(60.97, 6.39) * mm, "end": v(60.97, 10.64) * mm});
            skPoint(sketch, "E124.118", {"position": v(58.48, 0) * mm});
            skPoint(sketch, "E124.119", {"position": v(60.97, -7.6) * mm});
            skLineSegment(sketch, "E124.120", {"start": v(72.74, 0) * mm, "end": v(72.74, -0.02) * mm});
            skPoint(sketch, "E124.121", {"position": v(60.97, 16.3) * mm});
            skArc(sketch, "E124.122", {"start": v(66.63, 16.3) * mm, "mid": v(62.63, 14.65) * mm, "end": v(60.97, 10.64) * mm});
            skPoint(sketch, "E124.123", {"position": v(110.29, -6.24) * mm});
            skArc(sketch, "E124.124", {"start": v(104.63, -6.24) * mm, "mid": v(108.63, -4.58) * mm, "end": v(110.29, -0.58) * mm});
            skPoint(sketch, "E124.125", {"position": v(60.97, -6.24) * mm});
            skArc(sketch, "E124.126", {"start": v(60.97, -2.2) * mm, "mid": v(62.16, -5.06) * mm, "end": v(65.01, -6.24) * mm});
            skPoint(sketch, "E124.127", {"position": v(110.29, 16.3) * mm});
            skArc(sketch, "E124.128", {"start": v(110.29, 12.6) * mm, "mid": v(109.2, 15.22) * mm, "end": v(106.59, 16.3) * mm});
            skPoint(sketch, "E124.129", {"position": v(110.29, 7.43) * mm});
            skArc(sketch, "E124.130", {"start": v(110.29, 3.72) * mm, "mid": v(109.2, 6.34) * mm, "end": v(106.59, 7.43) * mm});
            skPoint(sketch, "E124.131", {"position": v(60.97, 2.69) * mm});
            skArc(sketch, "E124.132", {"start": v(60.97, 6.39) * mm, "mid": v(62.06, 3.77) * mm, "end": v(64.67, 2.69) * mm});
            skPoint(sketch, "E124.133", {"position": v(60.97, 0) * mm});
            skArc(sketch, "E124.134", {"start": v(62.77, 0) * mm, "mid": v(61.5, -0.53) * mm, "end": v(60.97, -1.8) * mm});
            skPoint(sketch, "E124.135", {"position": v(110.29, 10.1) * mm});
            skArc(sketch, "E124.136", {"start": v(108.44, 10.1) * mm, "mid": v(109.75, 10.65) * mm, "end": v(110.29, 11.96) * mm});
            skLineSegment(sketch, "E124.137", {"start": v(72.17, 9.5) * mm, "end": v(72.17, 9.4) * mm});
            skPoint(sketch, "E124.138", {"position": v(72.17, 11.49) * mm});
            skArc(sketch, "E124.139", {"start": v(74.15, 11.49) * mm, "mid": v(72.75, 10.9) * mm, "end": v(72.17, 9.5) * mm});
            skPoint(sketch, "E124.140", {"position": v(72.17, 7.43) * mm});
            skArc(sketch, "E124.141", {"start": v(72.17, 9.4) * mm, "mid": v(72.75, 8) * mm, "end": v(74.15, 7.43) * mm});
            skLineSegment(sketch, "E124.142", {"start": v(99.2, 0.7) * mm, "end": v(99.2, 0.63) * mm});
            skPoint(sketch, "E124.143", {"position": v(99.2, 2.69) * mm});
            skArc(sketch, "E124.144", {"start": v(99.2, 0.7) * mm, "mid": v(98.63, 2.1) * mm, "end": v(97.22, 2.69) * mm});
            skPoint(sketch, "E124.145", {"position": v(99.2, -1.35) * mm});
            skArc(sketch, "E124.146", {"start": v(97.22, -1.35) * mm, "mid": v(98.63, -0.77) * mm, "end": v(99.2, 0.63) * mm});
            skPoint(sketch, "E124.147", {"position": v(72.74, -1.35) * mm});
            skArc(sketch, "E124.148", {"start": v(72.74, -0.02) * mm, "mid": v(73.13, -0.96) * mm, "end": v(74.07, -1.35) * mm});
            skPoint(sketch, "E124.149", {"position": v(98.63, 11.49) * mm});
            skArc(sketch, "E124.150", {"start": v(98.63, 10.12) * mm, "mid": v(98.23, 11.09) * mm, "end": v(97.27, 11.49) * mm});
            skPoint(sketch, "E124.151", {"position": v(111.66, 16.3) * mm});
            skPoint(sketch, "E124.152", {"position": v(111.66, -6.24) * mm});
            skPoint(sketch, "E124.153", {"position": v(161, -6.24) * mm});
            skPoint(sketch, "E124.154", {"position": v(161, 16.3) * mm});
            skLineSegment(sketch, "E124.155", {"start": v(116.55, 16.3) * mm, "end": v(156.97, 16.3) * mm});
            skLineSegment(sketch, "E124.156", {"start": v(116.55, -6.24) * mm, "end": v(156.97, -6.24) * mm});
            skLineSegment(sketch, "E124.157", {"start": v(111.66, 11.41) * mm, "end": v(111.66, -1.35) * mm});
            skLineSegment(sketch, "E124.158", {"start": v(161, 12.27) * mm, "end": v(161, 11.93) * mm});
            skLineSegment(sketch, "E124.159", {"start": v(122.87, 5.48) * mm, "end": v(122.87, 10.24) * mm});
            skLineSegment(sketch, "E124.160", {"start": v(158.97, 0) * mm, "end": v(149.12, 0) * mm});
            skLineSegment(sketch, "E124.161", {"start": v(157.34, 10.13) * mm, "end": v(149.12, 10.13) * mm});
            skLineSegment(sketch, "E124.162", {"start": v(157.34, 10.13) * mm, "end": v(159.2, 10.13) * mm});
            skLineSegment(sketch, "E124.163", {"start": v(139.85, 11.56) * mm, "end": v(124.18, 11.56) * mm});
            skLineSegment(sketch, "E124.164", {"start": v(139.85, 11.56) * mm, "end": v(147.8, 11.56) * mm});
            skLineSegment(sketch, "E124.165", {"start": v(149.12, 10.13) * mm, "end": v(149.12, 10.24) * mm});
            skLineSegment(sketch, "E124.166", {"start": v(161, -2.03) * mm, "end": v(161, -2.21) * mm});
            skPoint(sketch, "E124.167", {"position": v(111.66, 16.3) * mm});
            skArc(sketch, "E124.168", {"start": v(116.55, 16.3) * mm, "mid": v(113.1, 14.87) * mm, "end": v(111.66, 11.41) * mm});
            skPoint(sketch, "E124.169", {"position": v(111.66, -6.24) * mm});
            skArc(sketch, "E124.170", {"start": v(111.66, -1.35) * mm, "mid": v(113.1, -4.8) * mm, "end": v(116.55, -6.24) * mm});
            skPoint(sketch, "E124.171", {"position": v(161, 16.3) * mm});
            skArc(sketch, "E124.172", {"start": v(161, 12.27) * mm, "mid": v(159.82, 15.12) * mm, "end": v(156.97, 16.3) * mm});
            skPoint(sketch, "E124.173", {"position": v(161, -6.24) * mm});
            skArc(sketch, "E124.174", {"start": v(156.97, -6.24) * mm, "mid": v(159.82, -5.06) * mm, "end": v(161, -2.21) * mm});
            skPoint(sketch, "E124.175", {"position": v(161, 10.13) * mm});
            skArc(sketch, "E124.176", {"start": v(159.2, 10.13) * mm, "mid": v(160.48, 10.66) * mm, "end": v(161, 11.93) * mm});
            skPoint(sketch, "E124.177", {"position": v(161, 0) * mm});
            skArc(sketch, "E124.178", {"start": v(161, -2.03) * mm, "mid": v(160.4, -0.6) * mm, "end": v(158.97, 0) * mm});
            skLineSegment(sketch, "E124.179", {"start": v(122.87, 5.48) * mm, "end": v(122.87, -0.2) * mm});
            skLineSegment(sketch, "E124.180", {"start": v(129.73, -1.52) * mm, "end": v(124.18, -1.52) * mm});
            skLineSegment(sketch, "E124.181", {"start": v(129.73, -1.52) * mm, "end": v(147.8, -1.52) * mm});
            skLineSegment(sketch, "E124.182", {"start": v(149.12, 0) * mm, "end": v(149.12, -0.2) * mm});
            skPoint(sketch, "E124.183", {"position": v(149.12, 11.56) * mm});
            skArc(sketch, "E124.184", {"start": v(149.12, 10.24) * mm, "mid": v(148.73, 11.17) * mm, "end": v(147.8, 11.56) * mm});
            skPoint(sketch, "E124.185", {"position": v(149.12, -1.52) * mm});
            skArc(sketch, "E124.186", {"start": v(147.8, -1.52) * mm, "mid": v(148.73, -1.14) * mm, "end": v(149.12, -0.2) * mm});
            skPoint(sketch, "E124.187", {"position": v(122.87, 11.56) * mm});
            skArc(sketch, "E124.188", {"start": v(124.18, 11.56) * mm, "mid": v(123.25, 11.17) * mm, "end": v(122.87, 10.24) * mm});
            skPoint(sketch, "E124.189", {"position": v(122.87, -1.52) * mm});
            skArc(sketch, "E124.190", {"start": v(122.87, -0.2) * mm, "mid": v(123.25, -1.14) * mm, "end": v(124.18, -1.52) * mm});
            skLineSegment(sketch, "E124.191", {"start": v(-0.53, 19.68) * mm, "end": v(0.96, 19.68) * mm});
            skLineSegment(sketch, "E124.192", {"start": v(-0.33, 15.35) * mm, "end": v(0.96, 15.35) * mm});
            skLineSegment(sketch, "E124.193.0", {"start": v(-2.03, 15.35) * mm, "end": v(-0.33, 15.35) * mm});
            skLineSegment(sketch, "E124.193.1", {"start": v(-0.33, 15.35) * mm, "end": v(0.96, 15.35) * mm});
            skLineSegment(sketch, "E124.193.2", {"start": v(0.96, 15.35) * mm, "end": v(0.96, 19.68) * mm});
            skLineSegment(sketch, "E124.193.3", {"start": v(0.96, 19.68) * mm, "end": v(-0.53, 19.68) * mm});
            skLineSegment(sketch, "E124.193.4", {"start": v(-0.53, 19.68) * mm, "end": v(-2.03, 19.68) * mm});
            skLineSegment(sketch, "E124.193.5", {"start": v(-2.03, 19.68) * mm, "end": v(-2.03, 31.6) * mm});
            skLineSegment(sketch, "E124.193.6", {"start": v(-2.03, 31.6) * mm, "end": v(-12.94, 31.6) * mm});
            skLineSegment(sketch, "E124.193.7", {"start": v(-12.94, 31.6) * mm, "end": v(-12.94, 19.68) * mm});
            skLineSegment(sketch, "E124.193.8", {"start": v(-12.94, 19.68) * mm, "end": v(-30.43, 19.68) * mm});
            skArc(sketch, "E124.193.9", {"start": v(-30.43, 19.68) * mm, "mid": v(-31.35, 20.2) * mm, "end": v(-31.35, 21.25) * mm});
            skLineSegment(sketch, "E124.193.10", {"start": v(-31.35, 21.25) * mm, "end": v(-25.18, 31.6) * mm});
            skLineSegment(sketch, "E124.193.11", {"start": v(-25.18, 31.6) * mm, "end": v(-31.25, 31.6) * mm});
            skLineSegment(sketch, "E124.193.12", {"start": v(-31.25, 31.6) * mm, "end": v(-35.26, 31.6) * mm});
            skLineSegment(sketch, "E124.193.13", {"start": v(-35.26, 31.6) * mm, "end": v(-42.35, 19.59) * mm});
            skArc(sketch, "E124.193.14", {"start": v(-42.35, 19.59) * mm, "mid": v(-42.25, 16.75) * mm, "end": v(-39.77, 15.35) * mm});
            skLineSegment(sketch, "E124.193.15", {"start": v(-39.77, 15.35) * mm, "end": v(-12.94, 15.35) * mm});
            skLineSegment(sketch, "E124.193.16", {"start": v(-12.94, 15.35) * mm, "end": v(-12.94, 11.72) * mm});
            skLineSegment(sketch, "E124.193.17", {"start": v(-12.94, 11.72) * mm, "end": v(-2.03, 11.72) * mm});
            skLineSegment(sketch, "E124.193.18", {"start": v(-2.03, 11.72) * mm, "end": v(-2.03, 15.35) * mm});
            skLineSegment(sketch, "E125", {"start": v(0.96, 19.1) * mm, "end": v(4.7, 19.1) * mm});
            skLineSegment(sketch, "E126", {"start": v(0.96, 15.95) * mm, "end": v(4.7, 15.95) * mm});
            skLineSegment(sketch, "E127", {"start": v(3.28, 19.1) * mm, "end": v(0.96, 19.1) * mm});
            skLineSegment(sketch, "E128", {"start": v(-41.74, 16.12) * mm, "end": v(-52.01, 16.17) * mm});
            skLineSegment(sketch, "E129.trimOffspring", {"start": v(-62.04, 19.1) * mm, "end": v(-65.54, 19.1) * mm});
            skLineSegment(sketch, "E130.trimOffspring", {"start": v(-62.04, 16.2) * mm, "end": v(-65.54, 16.22) * mm});
            skLineSegment(sketch, "E131.trimOffspring", {"start": v(-42.55, 19.1) * mm, "end": v(-52.01, 19.1) * mm});
            skArc(sketch, "E132.0", {"start": v(66.63, 17.15) * mm, "mid": v(62.43, 15.61) * mm, "end": v(60.21, 11.72) * mm});
            skLineSegment(sketch, "E132.1", {"start": v(67.75, 17.15) * mm, "end": v(66.63, 17.15) * mm});
            skLineSegment(sketch, "E133", {"start": v(60.21, 11.72) * mm, "end": v(61.08, 11.72) * mm});
            skLineSegment(sketch, "E134", {"start": v(67.75, 17.15) * mm, "end": v(67.75, 16.3) * mm});
            skLineSegment(sketch, "E135", {"start": v(110.27, -1.1) * mm, "end": v(111.66, -1.1) * mm});
            skLineSegment(sketch, "E136", {"start": v(110.29, 3.72) * mm, "end": v(111.66, 3.72) * mm});
            skPoint(sketch, "E137", {"position": v(20.61, 19.1) * mm});
            skPoint(sketch, "E138", {"position": v(20.61, 15.95) * mm});
            skLineSegment(sketch, "E139", {"start": v(20.61, 19.1) * mm, "end": v(20.61, 15.95) * mm});
            skLineSegment(sketch, "E140", {"start": v(24.38, 19.1) * mm, "end": v(24.38, 16.28) * mm});
            skLineSegment(sketch, "E141", {"start": v(20.61, 19.1) * mm, "end": v(24.38, 19.1) * mm});
            skLineSegment(sketch, "E142", {"start": v(20.61, 15.95) * mm, "end": v(24.4, 15.95) * mm});
            skSolve(sketch);
        }
        {
            var Q0;
            Q0 = qSketchRegion(id + "F0", true);
            extrude(context, id + "F2", {"entities" : qUnion([Q0]), "depth" : 4 * mm, "offsetDistance" : 25 * mm});
        }
        {
            var Q0;
            {var subQ2=sQuery(id+"F1.wireOp",EDGE,"E129.trimOffspring");Q0=makeQuery(id+"F1.imprint","IMPRINT",FACE,{"disambiguationData":[TD([[makeQuery(id+"F1.imprint","IMPRINT",EDGE,{"derivedFrom":subQ2}),1.0]])]});}
            var Q1;
            {var subQ0=sQuery(id+"F1.wireOp",EDGE,"E128");Q1=makeQuery(id+"F1.imprint","IMPRINT",FACE,{"disambiguationData":[TD([[makeQuery(id+"F1.imprint","IMPRINT",EDGE,{"derivedFrom":subQ0}),-1.0]])]});}
            var Q2;
            {var subQ5=sQuery(id+"F1.wireOp",EDGE,"E127");Q2=makeQuery(id+"F1.imprint","IMPRINT",FACE,{"disambiguationData":[TD([[makeQuery(id+"F1.imprint","IMPRINT",EDGE,{"derivedFrom":subQ5}),1.0]])]});}
            var Q3;
            Q3=makeQuery(id+"F1.imprint","IMPRINT",FACE,{"disambiguationData":[TD([[makeQuery(id+"F1.imprint","IMPRINT",EDGE,{"derivedFrom":sQuery(id+"F1.wireOp",EDGE,"E132.0")}),1.0]])]});
            var Q4;
            {var subQ4=sQuery(id+"F1.wireOp",EDGE,"E124.102");Q4=makeQuery(id+"F1.imprint","IMPRINT",FACE,{"disambiguationData":[TD([[makeQuery(id+"F1.imprint","IMPRINT",EDGE,{"derivedFrom":subQ4}),1.0]])]});}
            var Q5;
            Q5=makeQuery(id+"F1.imprint","IMPRINT",FACE,{"disambiguationData":[TD([[makeQuery(id+"F1.imprint","IMPRINT",EDGE,{"derivedFrom":sQuery(id+"F1.wireOp",EDGE,"E139")}),1.0]])]});
            extrude(context, id + "F3", {"entities" : qUnion([Q0, Q1, Q2, Q3, Q4, Q5]), "depth" : 1.5 * mm, "offsetDistance" : 25 * mm});
        }
        {
            var Q0;
            Q0=makeQuery(id+"F0.imprint","IMPRINT",FACE,{"disambiguationData":[TD([[makeQuery(id+"F0.imprint","IMPRINT",EDGE,{"derivedFrom":sQuery(id+"F0.wireOp",EDGE,"E95.bottom")}),-1.0]])]});
            var sketch = newSketch(context, id + "F4", { "sketchPlane" : qUnion([Q0])});
            skCircle(sketch, "E143", {"center": v(117.53, 10.41) * mm, "radius": 4 * mm});
            skCircle(sketch, "E144", {"center": v(103.95, -1.2) * mm, "radius": 4 * mm});
            skCircle(sketch, "E145", {"center": v(29.55, 21.82) * mm, "radius": 4 * mm});
            skCircle(sketch, "E146", {"center": v(-7.46, 17.6) * mm, "radius": 4 * mm});
            skCircle(sketch, "E147", {"center": v(-57.22, 22.35) * mm, "radius": 4 * mm});
            skCircle(sketch, "E148", {"center": v(-104.26, 25.15) * mm, "radius": 4 * mm});
            skCircle(sketch, "E149", {"center": v(156.18, 13.42) * mm, "radius": 2 * mm});
            skCircle(sketch, "E150", {"center": v(156.68, -2.9) * mm, "radius": 2 * mm});
            skCircle(sketch, "E151", {"center": v(66.93, -3.1) * mm, "radius": 2 * mm});
            skCircle(sketch, "E152", {"center": v(62.65, 20.28) * mm, "radius": 2 * mm});
            skCircle(sketch, "E153", {"center": v(-32.81, 27.25) * mm, "radius": 2 * mm});
            skCircle(sketch, "E154", {"center": v(-72.55, 14.76) * mm, "radius": 2 * mm});
            skSolve(sketch);
        }
        {
            var Q0;
            Q0=makeQuery(id+"F4.imprint","IMPRINT",FACE,{"disambiguationData":[TD([[makeQuery(id+"F4.imprint","IMPRINT",EDGE,{"derivedFrom":sQuery(id+"F4.wireOp",EDGE,"E149")}),1.0]])]});
            var Q1;
            Q1=makeQuery(id+"F4.imprint","IMPRINT",FACE,{"disambiguationData":[TD([[makeQuery(id+"F4.imprint","IMPRINT",EDGE,{"derivedFrom":sQuery(id+"F4.wireOp",EDGE,"E150")}),1.0]])]});
            var Q2;
            Q2=makeQuery(id+"F4.imprint","IMPRINT",FACE,{"disambiguationData":[TD([[makeQuery(id+"F4.imprint","IMPRINT",EDGE,{"derivedFrom":sQuery(id+"F4.wireOp",EDGE,"E151")}),1.0]])]});
            var Q3;
            Q3=makeQuery(id+"F4.imprint","IMPRINT",FACE,{"disambiguationData":[TD([[makeQuery(id+"F4.imprint","IMPRINT",EDGE,{"derivedFrom":sQuery(id+"F4.wireOp",EDGE,"E152")}),1.0]])]});
            var Q4;
            Q4=makeQuery(id+"F4.imprint","IMPRINT",FACE,{"disambiguationData":[TD([[makeQuery(id+"F4.imprint","IMPRINT",EDGE,{"derivedFrom":sQuery(id+"F4.wireOp",EDGE,"E153")}),1.0]])]});
            var Q5;
            Q5=makeQuery(id+"F4.imprint","IMPRINT",FACE,{"disambiguationData":[TD([[makeQuery(id+"F4.imprint","IMPRINT",EDGE,{"derivedFrom":sQuery(id+"F4.wireOp",EDGE,"E154")}),1.0]])]});
            var Q6;
            Q6=sQuery(id+"F4.wireOp",EDGE,"E149");
            var Q7;
            Q7=sQuery(id+"F4.wireOp",EDGE,"E150");
            var Q8;
            Q8=sQuery(id+"F4.wireOp",EDGE,"E151");
            var Q9;
            Q9=sQuery(id+"F4.wireOp",EDGE,"E152");
            var Q10;
            Q10=sQuery(id+"F4.wireOp",EDGE,"E153");
            var Q11;
            Q11=sQuery(id+"F4.wireOp",EDGE,"E154");
            extrude(context, id + "F5", {"entities" : qUnion([Q0, Q1, Q2, Q3, Q4, Q5]), "operationType" : NewBodyOperationType.REMOVE, "surfaceEntities" : qUnion([Q6, Q7, Q8, Q9, Q10, Q11]), "depth" : 1 * mm, "offsetDistance" : 25 * mm});
        }
        {
            var Q0;
            Q0=makeQuery(id+"F4.imprint","IMPRINT",FACE,{"disambiguationData":[TD([[makeQuery(id+"F4.imprint","IMPRINT",EDGE,{"derivedFrom":sQuery(id+"F4.wireOp",EDGE,"E143")}),1.0]])]});
            var Q1;
            Q1=makeQuery(id+"F4.imprint","IMPRINT",FACE,{"disambiguationData":[TD([[makeQuery(id+"F4.imprint","IMPRINT",EDGE,{"derivedFrom":sQuery(id+"F4.wireOp",EDGE,"E144")}),1.0]])]});
            var Q2;
            Q2=makeQuery(id+"F4.imprint","IMPRINT",FACE,{"disambiguationData":[TD([[makeQuery(id+"F4.imprint","IMPRINT",EDGE,{"derivedFrom":sQuery(id+"F4.wireOp",EDGE,"E145")}),1.0]])]});
            var Q3;
            Q3=makeQuery(id+"F4.imprint","IMPRINT",FACE,{"disambiguationData":[TD([[makeQuery(id+"F4.imprint","IMPRINT",EDGE,{"derivedFrom":sQuery(id+"F4.wireOp",EDGE,"E146")}),1.0]])]});
            var Q4;
            Q4=makeQuery(id+"F4.imprint","IMPRINT",FACE,{"disambiguationData":[TD([[makeQuery(id+"F4.imprint","IMPRINT",EDGE,{"derivedFrom":sQuery(id+"F4.wireOp",EDGE,"E147")}),1.0]])]});
            var Q5;
            Q5=makeQuery(id+"F4.imprint","IMPRINT",FACE,{"disambiguationData":[TD([[makeQuery(id+"F4.imprint","IMPRINT",EDGE,{"derivedFrom":sQuery(id+"F4.wireOp",EDGE,"E148")}),1.0]])]});
            extrude(context, id + "F6", {"entities" : qUnion([Q0, Q1, Q2, Q3, Q4, Q5]), "operationType" : NewBodyOperationType.REMOVE, "depth" : 2 * mm, "offsetDistance" : 25 * mm});
        }
        {
            var Q0;
            Q0=makeQuery(id+"F2.opExtrude","CAP_FACE",FACE,{"disambiguationData":[OSD([sQuery(id+"F0.wireOp",EDGE,"E4.bottom"),sQuery(id+"F0.wireOp",EDGE,"E4.top"),sQuery(id+"F0.wireOp",EDGE,"E4.left"),sQuery(id+"F0.wireOp",EDGE,"E4.right"),sQuery(id+"F0.wireOp",EDGE,"E5.bottom"),sQuery(id+"F0.wireOp",EDGE,"E5.top"),sQuery(id+"F0.wireOp",EDGE,"E5.right"),sQuery(id+"F0.wireOp",EDGE,"E6.bottom"),sQuery(id+"F0.wireOp",EDGE,"E6.top"),sQuery(id+"F0.wireOp",EDGE,"E6.left"),sQuery(id+"F0.wireOp",EDGE,"E6.right"),sQuery(id+"F0.wireOp",EDGE,"E7.filletArc"),sQuery(id+"F0.wireOp",EDGE,"E8.filletArc"),sQuery(id+"F0.wireOp",EDGE,"E9.filletArc"),sQuery(id+"F0.wireOp",EDGE,"E10.filletArc"),sQuery(id+"F0.wireOp",EDGE,"E11.filletArc"),sQuery(id+"F0.wireOp",EDGE,"E12.filletArc"),sQuery(id+"F0.wireOp",EDGE,"E13.filletArc"),sQuery(id+"F0.wireOp",EDGE,"E14.trimOffspring"),sQuery(id+"F0.wireOp",EDGE,"E15.filletArc")])],"isStart":false});
            var Q1;
            Q1=makeQuery(id+"F2.opExtrude","CAP_FACE",FACE,{"disambiguationData":[OSD([sQuery(id+"F0.wireOp",EDGE,"E16"),sQuery(id+"F0.wireOp",EDGE,"E17"),sQuery(id+"F0.wireOp",EDGE,"E18.left"),sQuery(id+"F0.wireOp",EDGE,"E18.right")])],"isStart":false});
            var Q2;
            Q2=makeQuery(id+"F2.opExtrude","CAP_FACE",FACE,{"disambiguationData":[OSD([sQuery(id+"F0.wireOp",EDGE,"E19"),sQuery(id+"F0.wireOp",EDGE,"E20.left"),sQuery(id+"F0.wireOp",EDGE,"E20.right"),sQuery(id+"F0.wireOp",EDGE,"E21.bottom"),sQuery(id+"F0.wireOp",EDGE,"E21.top"),sQuery(id+"F0.wireOp",EDGE,"E21.left"),sQuery(id+"F0.wireOp",EDGE,"E22"),sQuery(id+"F0.wireOp",EDGE,"E23"),sQuery(id+"F0.wireOp",EDGE,"E25.trimOffspring"),sQuery(id+"F0.wireOp",EDGE,"E26.trimOffspring"),sQuery(id+"F0.wireOp",EDGE,"E27.trimOffspring"),sQuery(id+"F0.wireOp",EDGE,"E28.trimOffspring"),sQuery(id+"F0.wireOp",EDGE,"E20.top"),sQuery(id+"F0.wireOp",EDGE,"E20.bottom"),sQuery(id+"F0.wireOp",EDGE,"E29.trimOffspring"),sQuery(id+"F0.wireOp",EDGE,"E30"),sQuery(id+"F0.wireOp",EDGE,"E31"),sQuery(id+"F0.wireOp",EDGE,"E118"),sQuery(id+"F0.wireOp",EDGE,"E119")])],"isStart":false});
            var Q3;
            Q3=makeQuery(id+"F2.opExtrude","CAP_FACE",FACE,{"disambiguationData":[OSD([sQuery(id+"F0.wireOp",EDGE,"E32"),sQuery(id+"F0.wireOp",EDGE,"E33"),sQuery(id+"F0.wireOp",EDGE,"E35"),sQuery(id+"F0.wireOp",EDGE,"E36"),sQuery(id+"F0.wireOp",EDGE,"E37"),sQuery(id+"F0.wireOp",EDGE,"E38.bottom"),sQuery(id+"F0.wireOp",EDGE,"E38.top"),sQuery(id+"F0.wireOp",EDGE,"E38.right"),sQuery(id+"F0.wireOp",EDGE,"E39.bottom"),sQuery(id+"F0.wireOp",EDGE,"E39.top"),sQuery(id+"F0.wireOp",EDGE,"E39.left"),sQuery(id+"F0.wireOp",EDGE,"E39.right"),sQuery(id+"F0.wireOp",EDGE,"E40.trimOffspring"),sQuery(id+"F0.wireOp",EDGE,"E41.filletArc"),sQuery(id+"F0.wireOp",EDGE,"E42.filletArc"),sQuery(id+"F0.wireOp",EDGE,"E43.filletArc"),sQuery(id+"F0.wireOp",EDGE,"E44.filletArc"),sQuery(id+"F0.wireOp",EDGE,"E45.filletArc"),sQuery(id+"F0.wireOp",EDGE,"E46.filletArc"),sQuery(id+"F0.wireOp",EDGE,"E47.filletArc"),sQuery(id+"F0.wireOp",EDGE,"E48.filletArc"),sQuery(id+"F0.wireOp",EDGE,"E49.filletArc"),sQuery(id+"F0.wireOp",EDGE,"E122.0"),sQuery(id+"F0.wireOp",EDGE,"E122.1"),sQuery(id+"F0.wireOp",EDGE,"E123")])],"isStart":false});
            var Q4;
            Q4=makeQuery(id+"F2.opExtrude","CAP_FACE",FACE,{"disambiguationData":[OSD([sQuery(id+"F0.wireOp",EDGE,"E50"),sQuery(id+"F0.wireOp",EDGE,"E51"),sQuery(id+"F0.wireOp",EDGE,"E52"),sQuery(id+"F0.wireOp",EDGE,"E53"),sQuery(id+"F0.wireOp",EDGE,"E54"),sQuery(id+"F0.wireOp",EDGE,"E55"),sQuery(id+"F0.wireOp",EDGE,"E56"),sQuery(id+"F0.wireOp",EDGE,"E57"),sQuery(id+"F0.wireOp",EDGE,"E58"),sQuery(id+"F0.wireOp",EDGE,"E59"),sQuery(id+"F0.wireOp",EDGE,"E60"),sQuery(id+"F0.wireOp",EDGE,"E61"),sQuery(id+"F0.wireOp",EDGE,"E62"),sQuery(id+"F0.wireOp",EDGE,"E63"),sQuery(id+"F0.wireOp",EDGE,"E64"),sQuery(id+"F0.wireOp",EDGE,"E65"),sQuery(id+"F0.wireOp",EDGE,"E66"),sQuery(id+"F0.wireOp",EDGE,"E67"),sQuery(id+"F0.wireOp",EDGE,"E68"),sQuery(id+"F0.wireOp",EDGE,"E69"),sQuery(id+"F0.wireOp",EDGE,"E70.trimOffspring"),sQuery(id+"F0.wireOp",EDGE,"E71.trimOffspring"),sQuery(id+"F0.wireOp",EDGE,"E74"),sQuery(id+"F0.wireOp",EDGE,"E75.filletArc"),sQuery(id+"F0.wireOp",EDGE,"E76.filletArc"),sQuery(id+"F0.wireOp",EDGE,"E77.filletArc"),sQuery(id+"F0.wireOp",EDGE,"E78.filletArc"),sQuery(id+"F0.wireOp",EDGE,"E79.filletArc"),sQuery(id+"F0.wireOp",EDGE,"E80.filletArc"),sQuery(id+"F0.wireOp",EDGE,"E81.filletArc"),sQuery(id+"F0.wireOp",EDGE,"E82.filletArc"),sQuery(id+"F0.wireOp",EDGE,"E83"),sQuery(id+"F0.wireOp",EDGE,"E84.filletArc"),sQuery(id+"F0.wireOp",EDGE,"E85.filletArc"),sQuery(id+"F0.wireOp",EDGE,"E86"),sQuery(id+"F0.wireOp",EDGE,"E87.filletArc"),sQuery(id+"F0.wireOp",EDGE,"E88.filletArc"),sQuery(id+"F0.wireOp",EDGE,"E89.filletArc"),sQuery(id+"F0.wireOp",EDGE,"E90.filletArc")])],"isStart":false});
            var Q5;
            Q5=makeQuery(id+"F2.opExtrude","CAP_FACE",FACE,{"disambiguationData":[OSD([sQuery(id+"F0.wireOp",EDGE,"E95.bottom"),sQuery(id+"F0.wireOp",EDGE,"E95.top"),sQuery(id+"F0.wireOp",EDGE,"E95.left"),sQuery(id+"F0.wireOp",EDGE,"E95.right"),sQuery(id+"F0.wireOp",EDGE,"E96"),sQuery(id+"F0.wireOp",EDGE,"E97"),sQuery(id+"F0.wireOp",EDGE,"E98"),sQuery(id+"F0.wireOp",EDGE,"E99"),sQuery(id+"F0.wireOp",EDGE,"E100"),sQuery(id+"F0.wireOp",EDGE,"E101"),sQuery(id+"F0.wireOp",EDGE,"E102"),sQuery(id+"F0.wireOp",EDGE,"E103.trimOffspring"),sQuery(id+"F0.wireOp",EDGE,"E104.filletArc"),sQuery(id+"F0.wireOp",EDGE,"E105.filletArc"),sQuery(id+"F0.wireOp",EDGE,"E106.filletArc"),sQuery(id+"F0.wireOp",EDGE,"E107.filletArc"),sQuery(id+"F0.wireOp",EDGE,"E108.filletArc"),sQuery(id+"F0.wireOp",EDGE,"E109.filletArc"),sQuery(id+"F0.wireOp",EDGE,"E110"),sQuery(id+"F0.wireOp",EDGE,"E111"),sQuery(id+"F0.wireOp",EDGE,"E112"),sQuery(id+"F0.wireOp",EDGE,"E113"),sQuery(id+"F0.wireOp",EDGE,"E114.filletArc"),sQuery(id+"F0.wireOp",EDGE,"E115.filletArc"),sQuery(id+"F0.wireOp",EDGE,"E116.filletArc"),sQuery(id+"F0.wireOp",EDGE,"E117.filletArc")])],"isStart":false});
            var Q6;
            Q6=makeQuery(id+"F2.opExtrude","CAP_FACE",FACE,{"disambiguationData":[OSD([sQuery(id+"F0.wireOp",EDGE,"E34.bottom"),sQuery(id+"F0.wireOp",EDGE,"E34.top"),sQuery(id+"F0.wireOp",EDGE,"E34.left"),sQuery(id+"F0.wireOp",EDGE,"E34.right")])],"isStart":false});
            fillet(context, id + "F7", {"entities" : qUnion([Q0, Q1, Q2, Q3, Q4, Q5, Q6]), "radius" : 1 * mm, "tangentPropagation" : true, "allowEdgeOverflow" : false});
        }
    });
